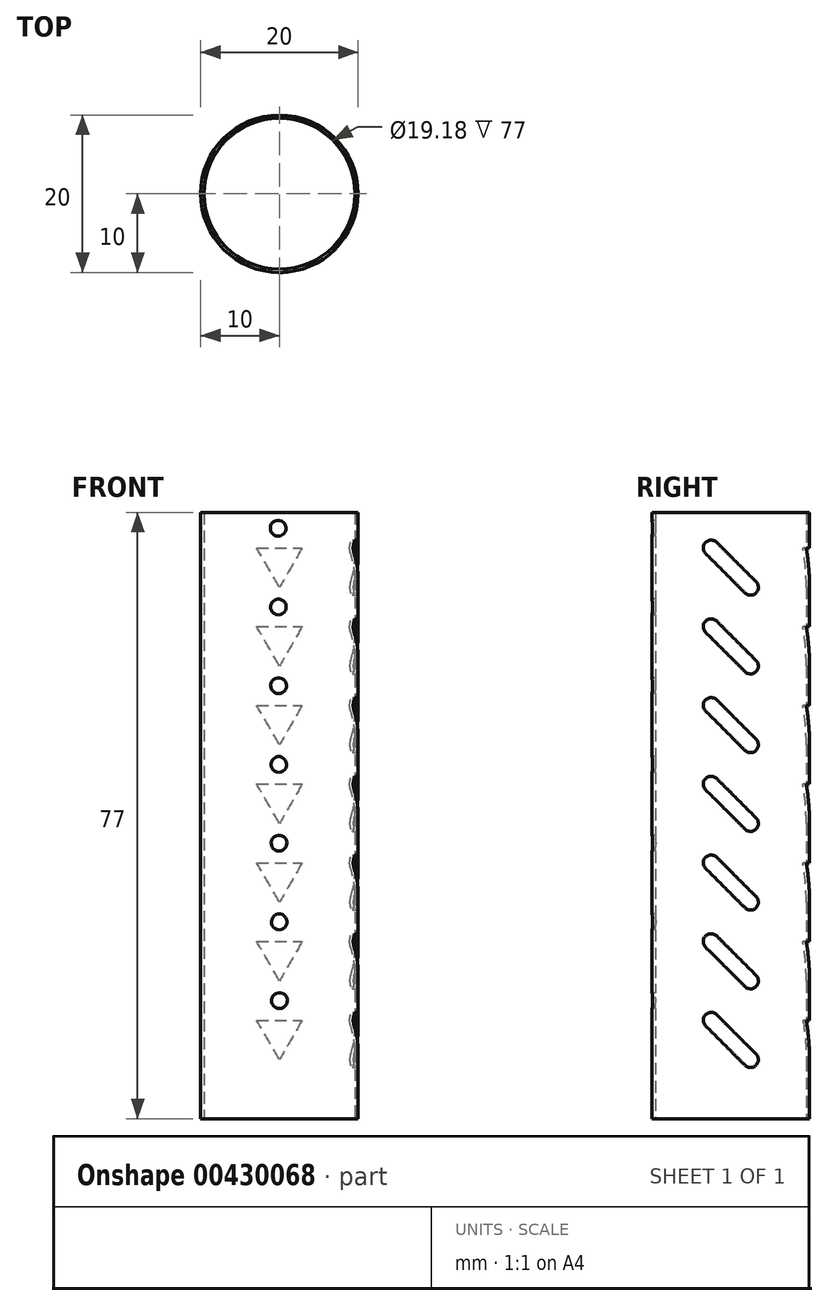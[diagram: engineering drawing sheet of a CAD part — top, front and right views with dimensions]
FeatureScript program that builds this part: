
annotation { "Feature Type Name" : "Feature", "Feature Type Description" : "" }
export const myFeature = defineFeature(function(context is Context, id is Id, definition is map)
    precondition{}
    {
        {
            var Q0;
            Q0=qCreatedBy(makeId("Top.planeOp"),FACE);
            var sketch = newSketch(context, id + "F0", { "sketchPlane" : qUnion([Q0])});
            skCircle(sketch, "E0", {"center": v(0, 0) * mm, "radius": 10 * mm});
            skCircle(sketch, "E1", {"center": v(0, 0) * mm, "radius": 9.6 * mm});
            skSolve(sketch);
        }
        {
            var Q0;
            Q0=makeQuery(id+"F0.imprint","IMPRINT",FACE,{"disambiguationData":[TD([[makeQuery(id+"F0.imprint","IMPRINT",EDGE,{"derivedFrom":sQuery(id+"F0.wireOp",EDGE,"E0")}),1.0]])]});
            extrude(context, id + "F1", {"entities" : qUnion([Q0]), "depth" : (7 * 10 + 7) * mm});
        }
        {
            var Q0;
            Q0=qCreatedBy(makeId("Front.planeOp"),FACE);
            cPlane(context, id + "F2", {"entities" : qUnion([Q0]), "cplaneType" : CPlaneType.OFFSET, "offset" : 10 * mm, "width" : 150 * mm, "height" : 150 * mm});
        }
        {
            var Q0;
            Q0=qCreatedBy(id+"F2.planeOp",FACE);
            var sketch = newSketch(context, id + "F3", { "sketchPlane" : qUnion([Q0])});
            skCircle(sketch, "E2", {"center": v(0, 15) * mm, "radius": 1 * mm});
            skCircle(sketch, "E3.1.0.0", {"center": v(-0.03, 25) * mm, "radius": 1 * mm});
            skCircle(sketch, "E3.2.0.0", {"center": v(-0.05, 35) * mm, "radius": 1 * mm});
            skCircle(sketch, "E3.3.0.0", {"center": v(-0.08, 45) * mm, "radius": 1 * mm});
            skCircle(sketch, "E3.4.0.0", {"center": v(-0.1, 55) * mm, "radius": 1 * mm});
            skCircle(sketch, "E3.5.0.0", {"center": v(-0.13, 65) * mm, "radius": 1 * mm});
            skCircle(sketch, "E3.6.0.0", {"center": v(-0.16, 75) * mm, "radius": 1 * mm});
            skLineSegment(sketch, "E3.direction1", {"start": v(0, 15) * mm, "end": v(-0.03, 25) * mm, "construction": true});
            skSolve(sketch);
        }
        {
            var Q0;
            Q0 = qSketchRegion(id + "F3", true);
            extrude(context, id + "F4", {"entities" : qUnion([Q0]), "operationType" : NewBodyOperationType.REMOVE, "oppositeDirection" : true, "depth" : 10 * mm});
        }
        {
            var Q0;
            Q0=qCreatedBy(makeId("Right.planeOp"),FACE);
            cPlane(context, id + "F5", {"entities" : qUnion([Q0]), "cplaneType" : CPlaneType.OFFSET, "offset" : 10 * mm, "width" : 150 * mm, "height" : 150 * mm});
        }
        {
            var Q0;
            Q0=qCreatedBy(id+"F5.planeOp",FACE);
            var sketch = newSketch(context, id + "F6", { "sketchPlane" : qUnion([Q0])});
            skLineSegment(sketch, "E4", {"start": v(-2.5, 12.5) * mm, "end": v(2.5, 7.5) * mm, "construction": true});
            skLineSegment(sketch, "E5", {"start": v(2.5, 7.5) * mm, "end": v(0, 7.5) * mm, "construction": true});
            skPoint(sketch, "E5.endSnap0", {"position": v(0, 10) * mm});
            skArc(sketch, "E6.0.startCap", {"start": v(-3.2, 11.8) * mm, "mid": v(-3.2, 13.2) * mm, "end": v(-1.8, 13.2) * mm});
            skArc(sketch, "E6.0.endCap", {"start": v(3.2, 8.2) * mm, "mid": v(3.2, 6.8) * mm, "end": v(1.8, 6.8) * mm});
            skLineSegment(sketch, "E6.0.left", {"start": v(-1.8, 13.2) * mm, "end": v(3.2, 8.2) * mm});
            skLineSegment(sketch, "E6.0.right", {"start": v(-3.2, 11.8) * mm, "end": v(1.8, 6.8) * mm});
            skLineSegment(sketch, "E7.1.0.0", {"start": v(-2.5, 22.5) * mm, "end": v(2.5, 17.5) * mm, "construction": true});
            skArc(sketch, "E7.1.0.1", {"start": v(-3.2, 21.8) * mm, "mid": v(-3.2, 23.2) * mm, "end": v(-1.8, 23.2) * mm});
            skLineSegment(sketch, "E7.1.0.2", {"start": v(-3.2, 21.8) * mm, "end": v(1.8, 16.8) * mm});
            skLineSegment(sketch, "E7.1.0.3", {"start": v(-1.8, 23.2) * mm, "end": v(3.2, 18.2) * mm});
            skLineSegment(sketch, "E7.1.0.4", {"start": v(2.5, 17.5) * mm, "end": v(0, 17.5) * mm, "construction": true});
            skPoint(sketch, "E7.1.0.5", {"position": v(0, 20) * mm});
            skArc(sketch, "E7.1.0.6", {"start": v(3.2, 18.2) * mm, "mid": v(3.2, 16.8) * mm, "end": v(1.8, 16.8) * mm});
            skLineSegment(sketch, "E7.2.0.0", {"start": v(-2.5, 32.5) * mm, "end": v(2.5, 27.5) * mm, "construction": true});
            skArc(sketch, "E7.2.0.1", {"start": v(-3.2, 31.8) * mm, "mid": v(-3.2, 33.2) * mm, "end": v(-1.8, 33.2) * mm});
            skLineSegment(sketch, "E7.2.0.2", {"start": v(-3.2, 31.8) * mm, "end": v(1.8, 26.8) * mm});
            skLineSegment(sketch, "E7.2.0.3", {"start": v(-1.8, 33.2) * mm, "end": v(3.2, 28.2) * mm});
            skLineSegment(sketch, "E7.2.0.4", {"start": v(2.5, 27.5) * mm, "end": v(0, 27.5) * mm, "construction": true});
            skPoint(sketch, "E7.2.0.5", {"position": v(0, 30) * mm});
            skArc(sketch, "E7.2.0.6", {"start": v(3.2, 28.2) * mm, "mid": v(3.2, 26.8) * mm, "end": v(1.8, 26.8) * mm});
            skLineSegment(sketch, "E7.3.0.0", {"start": v(-2.5, 42.5) * mm, "end": v(2.5, 37.5) * mm, "construction": true});
            skArc(sketch, "E7.3.0.1", {"start": v(-3.2, 41.8) * mm, "mid": v(-3.2, 43.2) * mm, "end": v(-1.8, 43.2) * mm});
            skLineSegment(sketch, "E7.3.0.2", {"start": v(-3.2, 41.8) * mm, "end": v(1.8, 36.8) * mm});
            skLineSegment(sketch, "E7.3.0.3", {"start": v(-1.8, 43.2) * mm, "end": v(3.2, 38.2) * mm});
            skLineSegment(sketch, "E7.3.0.4", {"start": v(2.5, 37.5) * mm, "end": v(0, 37.5) * mm, "construction": true});
            skPoint(sketch, "E7.3.0.5", {"position": v(0, 40) * mm});
            skArc(sketch, "E7.3.0.6", {"start": v(3.2, 38.2) * mm, "mid": v(3.2, 36.8) * mm, "end": v(1.8, 36.8) * mm});
            skLineSegment(sketch, "E7.4.0.0", {"start": v(-2.5, 52.5) * mm, "end": v(2.5, 47.5) * mm, "construction": true});
            skArc(sketch, "E7.4.0.1", {"start": v(-3.2, 51.8) * mm, "mid": v(-3.2, 53.2) * mm, "end": v(-1.8, 53.2) * mm});
            skLineSegment(sketch, "E7.4.0.2", {"start": v(-3.2, 51.8) * mm, "end": v(1.8, 46.8) * mm});
            skLineSegment(sketch, "E7.4.0.3", {"start": v(-1.8, 53.2) * mm, "end": v(3.2, 48.2) * mm});
            skLineSegment(sketch, "E7.4.0.4", {"start": v(2.5, 47.5) * mm, "end": v(0, 47.5) * mm, "construction": true});
            skPoint(sketch, "E7.4.0.5", {"position": v(0, 50) * mm});
            skArc(sketch, "E7.4.0.6", {"start": v(3.2, 48.2) * mm, "mid": v(3.2, 46.8) * mm, "end": v(1.8, 46.8) * mm});
            skLineSegment(sketch, "E7.5.0.0", {"start": v(-2.5, 62.5) * mm, "end": v(2.5, 57.5) * mm, "construction": true});
            skArc(sketch, "E7.5.0.1", {"start": v(-3.2, 61.8) * mm, "mid": v(-3.2, 63.2) * mm, "end": v(-1.8, 63.2) * mm});
            skLineSegment(sketch, "E7.5.0.2", {"start": v(-3.2, 61.8) * mm, "end": v(1.8, 56.8) * mm});
            skLineSegment(sketch, "E7.5.0.3", {"start": v(-1.8, 63.2) * mm, "end": v(3.2, 58.2) * mm});
            skLineSegment(sketch, "E7.5.0.4", {"start": v(2.5, 57.5) * mm, "end": v(0, 57.5) * mm, "construction": true});
            skPoint(sketch, "E7.5.0.5", {"position": v(0, 60) * mm});
            skArc(sketch, "E7.5.0.6", {"start": v(3.2, 58.2) * mm, "mid": v(3.2, 56.8) * mm, "end": v(1.8, 56.8) * mm});
            skLineSegment(sketch, "E7.6.0.0", {"start": v(-2.5, 72.5) * mm, "end": v(2.5, 67.5) * mm, "construction": true});
            skArc(sketch, "E7.6.0.1", {"start": v(-3.2, 71.8) * mm, "mid": v(-3.2, 73.2) * mm, "end": v(-1.8, 73.2) * mm});
            skLineSegment(sketch, "E7.6.0.2", {"start": v(-3.2, 71.8) * mm, "end": v(1.8, 66.8) * mm});
            skLineSegment(sketch, "E7.6.0.3", {"start": v(-1.8, 73.2) * mm, "end": v(3.2, 68.2) * mm});
            skLineSegment(sketch, "E7.6.0.4", {"start": v(2.5, 67.5) * mm, "end": v(0, 67.5) * mm, "construction": true});
            skPoint(sketch, "E7.6.0.5", {"position": v(0, 70) * mm});
            skArc(sketch, "E7.6.0.6", {"start": v(3.2, 68.2) * mm, "mid": v(3.2, 66.8) * mm, "end": v(1.8, 66.8) * mm});
            skLineSegment(sketch, "E7.direction1", {"start": v(0, 7.5) * mm, "end": v(0, 17.5) * mm, "construction": true});
            skSolve(sketch);
        }
        {
            var Q0;
            Q0 = qSketchRegion(id + "F6", true);
            extrude(context, id + "F7", {"entities" : qUnion([Q0]), "operationType" : NewBodyOperationType.REMOVE, "oppositeDirection" : true, "depth" : 10 * mm});
        }
        {
            var Q0;
            Q0=qCreatedBy(makeId("Front.planeOp"),FACE);
            cPlane(context, id + "F8", {"entities" : qUnion([Q0]), "cplaneType" : CPlaneType.OFFSET, "offset" : 10 * mm, "oppositeDirection" : true, "width" : 150 * mm, "height" : 150 * mm});
        }
        {
            var Q0;
            Q0=qCreatedBy(id+"F8.planeOp",FACE);
            var sketch = newSketch(context, id + "F9", { "sketchPlane" : qUnion([Q0])});
            skLineSegment(sketch, "E8", {"start": v(-2.89, 12.5) * mm, "end": v(0, 7.5) * mm});
            skLineSegment(sketch, "E9", {"start": v(0, 7.5) * mm, "end": v(2.89, 12.5) * mm});
            skLineSegment(sketch, "E10", {"start": v(2.89, 12.5) * mm, "end": v(-2.89, 12.5) * mm});
            skLineSegment(sketch, "E11.1.0.0", {"start": v(0, 17.5) * mm, "end": v(2.89, 22.5) * mm});
            skLineSegment(sketch, "E11.1.0.1", {"start": v(2.89, 22.5) * mm, "end": v(-2.89, 22.5) * mm});
            skLineSegment(sketch, "E11.1.0.2", {"start": v(-2.89, 22.5) * mm, "end": v(0, 17.5) * mm});
            skLineSegment(sketch, "E11.2.0.0", {"start": v(0, 27.5) * mm, "end": v(2.89, 32.5) * mm});
            skLineSegment(sketch, "E11.2.0.1", {"start": v(2.89, 32.5) * mm, "end": v(-2.89, 32.5) * mm});
            skLineSegment(sketch, "E11.2.0.2", {"start": v(-2.89, 32.5) * mm, "end": v(0, 27.5) * mm});
            skLineSegment(sketch, "E11.3.0.0", {"start": v(0, 37.5) * mm, "end": v(2.89, 42.5) * mm});
            skLineSegment(sketch, "E11.3.0.1", {"start": v(2.89, 42.5) * mm, "end": v(-2.89, 42.5) * mm});
            skLineSegment(sketch, "E11.3.0.2", {"start": v(-2.89, 42.5) * mm, "end": v(0, 37.5) * mm});
            skLineSegment(sketch, "E11.4.0.0", {"start": v(0, 47.5) * mm, "end": v(2.89, 52.5) * mm});
            skLineSegment(sketch, "E11.4.0.1", {"start": v(2.89, 52.5) * mm, "end": v(-2.89, 52.5) * mm});
            skLineSegment(sketch, "E11.4.0.2", {"start": v(-2.89, 52.5) * mm, "end": v(0, 47.5) * mm});
            skLineSegment(sketch, "E11.5.0.0", {"start": v(0, 57.5) * mm, "end": v(2.89, 62.5) * mm});
            skLineSegment(sketch, "E11.5.0.1", {"start": v(2.89, 62.5) * mm, "end": v(-2.89, 62.5) * mm});
            skLineSegment(sketch, "E11.5.0.2", {"start": v(-2.89, 62.5) * mm, "end": v(0, 57.5) * mm});
            skLineSegment(sketch, "E11.6.0.0", {"start": v(0, 67.5) * mm, "end": v(2.89, 72.5) * mm});
            skLineSegment(sketch, "E11.6.0.1", {"start": v(2.89, 72.5) * mm, "end": v(-2.89, 72.5) * mm});
            skLineSegment(sketch, "E11.6.0.2", {"start": v(-2.89, 72.5) * mm, "end": v(0, 67.5) * mm});
            skLineSegment(sketch, "E11.direction1", {"start": v(0, 7.5) * mm, "end": v(0, 17.5) * mm, "construction": true});
            skSolve(sketch);
        }
        {
            var Q0;
            Q0 = qSketchRegion(id + "F9", true);
            extrude(context, id + "F10", {"entities" : qUnion([Q0]), "operationType" : NewBodyOperationType.REMOVE, "depth" : 10 * mm});
        }
    });
